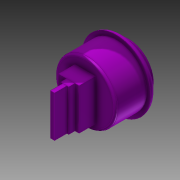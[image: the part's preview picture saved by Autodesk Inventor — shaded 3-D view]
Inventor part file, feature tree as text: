
AUTODESK INVENTOR PART (.ipt)
format: ipt  version: 2013 (Build 170138000, 138)  size: 183,296 bytes
history: native  units: mm
features: extrude x6, sketch x6, fillet x3
ambient origin geometry x8: Origin, YZ Plane, XZ Plane, XY Plane, X Axis, Y Axis, Z Axis, Center Point
bodies: Solid1 (feature_tree)
feature tree (15):
  extrude  "Extrusion1"  Depth=33.5mm
  extrude  "Extrusion2"  Depth=25.0mm TaperAngle=0.0deg
  fillet  "Fillet1"  Radius=1.5mm
  fillet  "Fillet2"  Radius=2.95mm
  extrude  "Extrusion5"  Depth=15.0mm TaperAngle=0.0deg
  extrude  "Extrusion7"  Depth=20.0mm
  extrude  "Extrusion8"  Depth=4.0mm
  extrude  "Extrusion10"  Depth=3.0mm TaperAngle=0.0deg
  fillet  "Fillet3"  Radius=6.0mm
  sketch  "Sketch1"  dims[d0=25.0mm d1=33.5mm]
  sketch  "Sketch2"  dims[d4=3.0mm d5=0.0mm d6=25.0mm d10=6.5mm d11=0.0mm d18=1.5mm d19=2.95mm]
  sketch  "Sketch5"  dims[d23=29.5mm d24=15.0mm d25=0.0mm]
  sketch  "Sketch7"  dims[d30=10.0mm d32=20.0mm]
  sketch  "Sketch8"  dims[d33=8.0mm d34=0.0mm d35=4.0mm]
  sketch  "Sketch10"  dims[d37=20.0mm d38=3.0mm d39=0.0mm d44=6.0mm d45=0.0mm d46=20.0mm d48=2.0mm d49=1.0mm]
